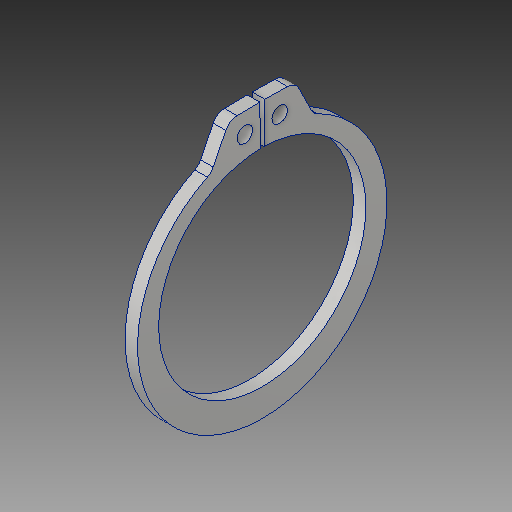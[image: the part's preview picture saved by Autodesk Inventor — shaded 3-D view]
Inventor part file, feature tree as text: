
AUTODESK INVENTOR PART (.ipt)
format: ipt  version: 2017 (Build 210142000, 142)  size: 111,616 bytes
history: native  units: in
note: dims shown in document units (in); Inventor stores cm internally (conversion verified against a paired STEP export)
features: fillet x1
ambient origin geometry x8: Origin, YZ Plane, XZ Plane, XY Plane, X Axis, Y Axis, Z Axis, Center Point
bodies: Solid1 (feature_tree)
feature tree (1):
  fillet  "Fillet1"  [1 undecoded]
note: 1 required parameter value undecoded (feature->parameter linkage not recoverable at this tier; creation-order binding heuristic only, values carry confidence <= 0.55)
